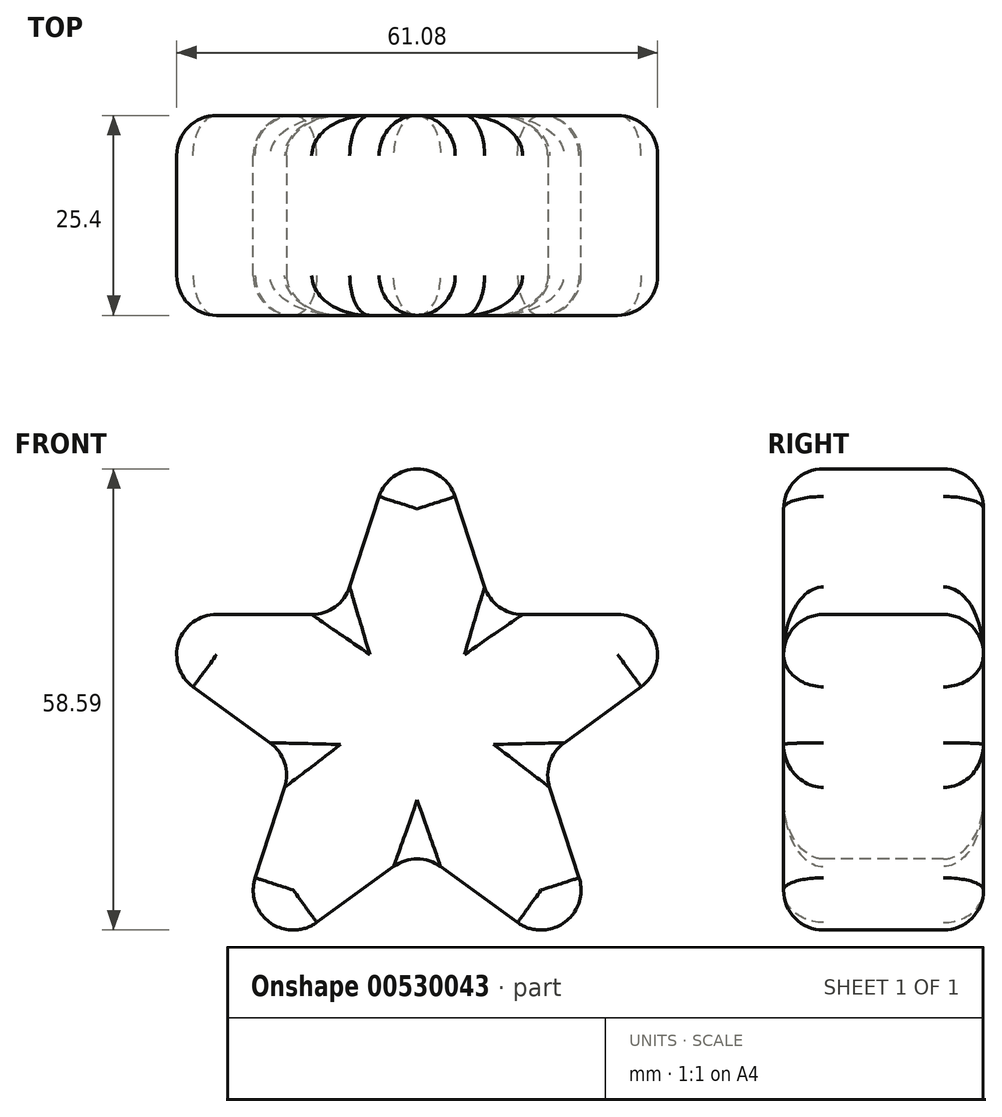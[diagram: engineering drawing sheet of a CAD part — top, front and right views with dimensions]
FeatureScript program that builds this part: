
annotation { "Feature Type Name" : "Feature", "Feature Type Description" : "" }
export const myFeature = defineFeature(function(context is Context, id is Id, definition is map)
    precondition{}
    {
        {
            var Q0;
            Q0=qCreatedBy(makeId("Front.planeOp"),FACE);
            var sketch = newSketch(context, id + "F0", { "sketchPlane" : qUnion([Q0])});
            skLineSegment(sketch, "E0", {"start": v(0, 29.86) * mm, "end": v(-41.1, 0) * mm});
            skLineSegment(sketch, "E1", {"start": v(0, 29.86) * mm, "end": v(41.1, 0) * mm});
            skLineSegment(sketch, "E2", {"start": v(-41.1, 0) * mm, "end": v(-25.4, -48.31) * mm});
            skLineSegment(sketch, "E3", {"start": v(-25.4, -48.31) * mm, "end": v(25.4, -48.31) * mm});
            skLineSegment(sketch, "E4", {"start": v(41.1, 0) * mm, "end": v(25.4, -48.31) * mm});
            skLineSegment(sketch, "E5", {"start": v(-25.4, -48.31) * mm, "end": v(0, 29.86) * mm});
            skLineSegment(sketch, "E6", {"start": v(0, 29.86) * mm, "end": v(25.4, -48.31) * mm});
            skLineSegment(sketch, "E7", {"start": v(25.4, -48.31) * mm, "end": v(-41.1, 0) * mm});
            skLineSegment(sketch, "E8", {"start": v(-41.1, 0) * mm, "end": v(41.1, 0) * mm});
            skLineSegment(sketch, "E9", {"start": v(41.1, 0) * mm, "end": v(-25.4, -48.31) * mm});
            skSolve(sketch);
        }
        {
            var Q0;
            {var subQ1=sQuery(id+"F0.wireOp",EDGE,"E5");var subQ3=sQuery(id+"F0.wireOp",EDGE,"E8");var subQ4=makeQuery(id+"F0.imprint","INTERSECT",VERTEX,{"derivedFrom":[subQ1,subQ3]});Q0=makeQuery(id+"F0.imprint","IMPRINT",FACE,{"disambiguationData":[TD([[makeQuery(id+"F0.imprint","IMPRINT",EDGE,{"disambiguationData":[TD([[subQ4,-1.0]])],"derivedFrom":subQ3}),1.0]])]});}
            var Q1;
            {var subQ0=sQuery(id+"F0.wireOp",EDGE,"E7");var subQ1=sQuery(id+"F0.wireOp",EDGE,"E5");var subQ2=makeQuery(id+"F0.imprint","INTERSECT",VERTEX,{"derivedFrom":[subQ1,subQ0]});Q1=makeQuery(id+"F0.imprint","IMPRINT",FACE,{"disambiguationData":[TD([[makeQuery(id+"F0.imprint","IMPRINT",EDGE,{"disambiguationData":[TD([[subQ2,-1.0]])],"derivedFrom":subQ1}),1.0]])]});}
            var Q2;
            {var subQ1=sQuery(id+"F0.wireOp",EDGE,"E5");var subQ5=sQuery(id+"F0.wireOp",EDGE,"E7");var subQ6=makeQuery(id+"F0.imprint","INTERSECT",VERTEX,{"derivedFrom":[subQ1,subQ5]});Q2=makeQuery(id+"F0.imprint","IMPRINT",FACE,{"disambiguationData":[TD([[makeQuery(id+"F0.imprint","IMPRINT",EDGE,{"disambiguationData":[TD([[subQ6,-1.0]])],"derivedFrom":subQ1}),-1.0]])]});}
            var Q3;
            {var subQ0=sQuery(id+"F0.wireOp",EDGE,"E8");var subQ1=sQuery(id+"F0.wireOp",EDGE,"E6");var subQ2=makeQuery(id+"F0.imprint","INTERSECT",VERTEX,{"derivedFrom":[subQ1,subQ0]});Q3=makeQuery(id+"F0.imprint","IMPRINT",FACE,{"disambiguationData":[TD([[makeQuery(id+"F0.imprint","IMPRINT",EDGE,{"disambiguationData":[TD([[subQ2,-1.0]])],"derivedFrom":subQ1}),1.0]])]});}
            var Q4;
            {var subQ1=sQuery(id+"F0.wireOp",EDGE,"E6");var subQ3=sQuery(id+"F0.wireOp",EDGE,"E9");var subQ4=makeQuery(id+"F0.imprint","INTERSECT",VERTEX,{"derivedFrom":[subQ1,subQ3]});Q4=makeQuery(id+"F0.imprint","IMPRINT",FACE,{"disambiguationData":[TD([[makeQuery(id+"F0.imprint","IMPRINT",EDGE,{"disambiguationData":[TD([[subQ4,-1.0]])],"derivedFrom":subQ3}),1.0]])]});}
            var Q5;
            {var subQ1=sQuery(id+"F0.wireOp",EDGE,"E5");var subQ3=sQuery(id+"F0.wireOp",EDGE,"E7");var subQ4=makeQuery(id+"F0.imprint","INTERSECT",VERTEX,{"derivedFrom":[subQ1,subQ3]});Q5=makeQuery(id+"F0.imprint","IMPRINT",FACE,{"disambiguationData":[TD([[makeQuery(id+"F0.imprint","IMPRINT",EDGE,{"disambiguationData":[TD([[subQ4,1.0]])],"derivedFrom":subQ3}),1.0]])]});}
            extrude(context, id + "F1", {"entities" : qUnion([Q0, Q1, Q2, Q3, Q4, Q5]), "depth" : 25.4 * mm, "offsetDistance" : 25.4 * mm});
        }
        {
            var Q0;
            Q0=makeQuery(id+"F1.opExtrude","CAP_FACE",FACE,{"disambiguationData":[OSD([sQuery(id+"F0.wireOp",EDGE,"E5"),sQuery(id+"F0.wireOp",EDGE,"E6"),sQuery(id+"F0.wireOp",EDGE,"E7"),sQuery(id+"F0.wireOp",EDGE,"E8"),sQuery(id+"F0.wireOp",EDGE,"E9")])],"isStart":true});
            var Q1;
            Q1=makeQuery(id+"F1.opExtrude","CAP_FACE",FACE,{"disambiguationData":[OSD([sQuery(id+"F0.wireOp",EDGE,"E5"),sQuery(id+"F0.wireOp",EDGE,"E6"),sQuery(id+"F0.wireOp",EDGE,"E7"),sQuery(id+"F0.wireOp",EDGE,"E8"),sQuery(id+"F0.wireOp",EDGE,"E9")])],"isStart":false});
            fillet(context, id + "F2", {"entities" : qUnion([Q0, Q1]), "radius" : 5.08 * mm, "tangentPropagation" : true, "allowEdgeOverflow" : false});
        }
        {
            var Q0;
            {var subQ0=sQuery(id+"F0.wireOp",EDGE,"E7");Q0=makeQuery(id+"F1.opExtrude","SWEPT_FACE",FACE,{"disambiguationData":[OSD([subQ0]),TDD([makeQuery(id+"F0.imprint","IMPRINT",EDGE,{"disambiguationData":[TD([[makeQuery(id+"F0.imprint","INTERSECT",VERTEX,{"derivedFrom":[subQ0,sQuery(id+"F0.wireOp",EDGE,"E9")]}),1.0]])],"derivedFrom":subQ0})])]});}
            var Q1;
            {var subQ0=sQuery(id+"F0.wireOp",EDGE,"E9");Q1=makeQuery(id+"F1.opExtrude","SWEPT_FACE",FACE,{"disambiguationData":[OSD([subQ0]),TDD([makeQuery(id+"F0.imprint","IMPRINT",EDGE,{"disambiguationData":[TD([[makeQuery(id+"F0.imprint","INTERSECT",VERTEX,{"derivedFrom":[sQuery(id+"F0.wireOp",EDGE,"E7"),subQ0]}),-1.0]])],"derivedFrom":subQ0})])]});}
            var Q2;
            {var subQ0=sQuery(id+"F0.wireOp",EDGE,"E5");Q2=makeQuery(id+"F1.opExtrude","SWEPT_FACE",FACE,{"disambiguationData":[OSD([subQ0]),TDD([makeQuery(id+"F0.imprint","IMPRINT",EDGE,{"disambiguationData":[TD([[makeQuery(id+"F0.imprint","INTERSECT",VERTEX,{"derivedFrom":[subQ0,sQuery(id+"F0.wireOp",EDGE,"E7")]}),1.0]])],"derivedFrom":subQ0})])]});}
            var Q3;
            {var subQ0=sQuery(id+"F0.wireOp",EDGE,"E7");Q3=makeQuery(id+"F1.opExtrude","SWEPT_FACE",FACE,{"disambiguationData":[OSD([subQ0]),TDD([makeQuery(id+"F0.imprint","IMPRINT",EDGE,{"disambiguationData":[TD([[makeQuery(id+"F0.imprint","INTERSECT",VERTEX,{"derivedFrom":[sQuery(id+"F0.wireOp",EDGE,"E5"),subQ0]}),-1.0]])],"derivedFrom":subQ0})])]});}
            var Q4;
            {var subQ0=sQuery(id+"F0.wireOp",EDGE,"E6");Q4=makeQuery(id+"F1.opExtrude","SWEPT_FACE",FACE,{"disambiguationData":[OSD([subQ0]),TDD([makeQuery(id+"F0.imprint","IMPRINT",EDGE,{"disambiguationData":[TD([[makeQuery(id+"F0.imprint","INTERSECT",VERTEX,{"derivedFrom":[subQ0,sQuery(id+"F0.wireOp",EDGE,"E9")]}),-1.0]])],"derivedFrom":subQ0})])]});}
            var Q5;
            {var subQ0=sQuery(id+"F0.wireOp",EDGE,"E9");Q5=makeQuery(id+"F1.opExtrude","SWEPT_FACE",FACE,{"disambiguationData":[OSD([subQ0]),TDD([makeQuery(id+"F0.imprint","IMPRINT",EDGE,{"disambiguationData":[TD([[makeQuery(id+"F0.imprint","INTERSECT",VERTEX,{"derivedFrom":[sQuery(id+"F0.wireOp",EDGE,"E6"),subQ0]}),1.0]])],"derivedFrom":subQ0})])]});}
            var Q6;
            {var subQ0=sQuery(id+"F0.wireOp",EDGE,"E8");Q6=makeQuery(id+"F1.opExtrude","SWEPT_FACE",FACE,{"disambiguationData":[OSD([subQ0]),TDD([makeQuery(id+"F0.imprint","IMPRINT",EDGE,{"disambiguationData":[TD([[makeQuery(id+"F0.imprint","INTERSECT",VERTEX,{"derivedFrom":[sQuery(id+"F0.wireOp",EDGE,"E6"),subQ0]}),-1.0]])],"derivedFrom":subQ0})])]});}
            fillet(context, id + "F3", {"entities" : qUnion([Q0, Q1, Q2, Q3, Q4, Q5, Q6]), "radius" : 5.08 * mm, "tangentPropagation" : true, "allowEdgeOverflow" : false});
        }
        {
            var Q0;
            {var subQ0=sQuery(id+"F0.wireOp",EDGE,"E5");var subQ1=makeQuery(id+"F0.imprint","IMPRINT",EDGE,{"disambiguationData":[TD([[makeQuery(id+"F0.imprint","INTERSECT",VERTEX,{"derivedFrom":[subQ0,sQuery(id+"F0.wireOp",EDGE,"E8")]}),-1.0]])],"derivedFrom":subQ0});Q0=makeQuery(id+"F2.opFillet","BLEND_EDGE",EDGE,{"blendedFrom":[makeQuery(id+"F1.opExtrude","CAP_EDGE",EDGE,{"disambiguationData":[OSD([subQ0]),TDD([subQ1])],"isStart":true}),makeQuery(id+"F1.opExtrude","SWEPT_FACE",FACE,{"disambiguationData":[OSD([subQ0]),TDD([subQ1])]})],"blendedInto":[makeQuery(id+"F1.opExtrude","SWEPT_FACE",FACE,{"disambiguationData":[OSD([subQ0]),TDD([subQ1])]})]});}
            var Q1;
            {var subQ0=sQuery(id+"F0.wireOp",EDGE,"E5");var subQ1=makeQuery(id+"F0.imprint","IMPRINT",EDGE,{"disambiguationData":[TD([[makeQuery(id+"F0.imprint","INTERSECT",VERTEX,{"derivedFrom":[subQ0,sQuery(id+"F0.wireOp",EDGE,"E8")]}),-1.0]])],"derivedFrom":subQ0});Q1=makeQuery(id+"F2.opFillet","BLEND_EDGE",EDGE,{"blendedFrom":[makeQuery(id+"F1.opExtrude","CAP_EDGE",EDGE,{"disambiguationData":[OSD([subQ0]),TDD([subQ1])],"isStart":false}),makeQuery(id+"F1.opExtrude","SWEPT_FACE",FACE,{"disambiguationData":[OSD([subQ0]),TDD([subQ1])]})],"blendedInto":[makeQuery(id+"F1.opExtrude","SWEPT_FACE",FACE,{"disambiguationData":[OSD([subQ0]),TDD([subQ1])]})]});}
            var Q2;
            {var subQ0=sQuery(id+"F0.wireOp",EDGE,"E5");Q2=makeQuery(id+"F2.opFillet","BLEND_FACE",FACE,{"disambiguationData":[OSD([subQ0]),TDD([makeQuery(id+"F1.opExtrude","CAP_EDGE",EDGE,{"disambiguationData":[OSD([subQ0]),TDD([makeQuery(id+"F0.imprint","IMPRINT",EDGE,{"disambiguationData":[TD([[makeQuery(id+"F0.imprint","INTERSECT",VERTEX,{"derivedFrom":[subQ0,sQuery(id+"F0.wireOp",EDGE,"E8")]}),-1.0]])],"derivedFrom":subQ0})])],"isStart":true})])]});}
            var Q3;
            {var subQ0=sQuery(id+"F0.wireOp",EDGE,"E6");var subQ1=makeQuery(id+"F0.imprint","IMPRINT",EDGE,{"disambiguationData":[TD([[makeQuery(id+"F0.imprint","INTERSECT",VERTEX,{"derivedFrom":[subQ0,sQuery(id+"F0.wireOp",EDGE,"E8")]}),1.0]])],"derivedFrom":subQ0});Q3=makeQuery(id+"F2.opFillet","BLEND_EDGE",EDGE,{"blendedFrom":[makeQuery(id+"F1.opExtrude","CAP_EDGE",EDGE,{"disambiguationData":[OSD([subQ0]),TDD([subQ1])],"isStart":true}),makeQuery(id+"F1.opExtrude","SWEPT_FACE",FACE,{"disambiguationData":[OSD([subQ0]),TDD([subQ1])]})],"blendedInto":[makeQuery(id+"F1.opExtrude","SWEPT_FACE",FACE,{"disambiguationData":[OSD([subQ0]),TDD([subQ1])]})]});}
            var Q4;
            {var subQ0=sQuery(id+"F0.wireOp",EDGE,"E6");Q4=makeQuery(id+"F1.opExtrude","SWEPT_FACE",FACE,{"disambiguationData":[OSD([subQ0]),TDD([makeQuery(id+"F0.imprint","IMPRINT",EDGE,{"disambiguationData":[TD([[makeQuery(id+"F0.imprint","INTERSECT",VERTEX,{"derivedFrom":[subQ0,sQuery(id+"F0.wireOp",EDGE,"E8")]}),1.0]])],"derivedFrom":subQ0})])]});}
            var Q5;
            {var subQ0=sQuery(id+"F0.wireOp",EDGE,"E6");Q5=makeQuery(id+"F2.opFillet","BLEND_FACE",FACE,{"disambiguationData":[OSD([subQ0]),TDD([makeQuery(id+"F1.opExtrude","CAP_EDGE",EDGE,{"disambiguationData":[OSD([subQ0]),TDD([makeQuery(id+"F0.imprint","IMPRINT",EDGE,{"disambiguationData":[TD([[makeQuery(id+"F0.imprint","INTERSECT",VERTEX,{"derivedFrom":[subQ0,sQuery(id+"F0.wireOp",EDGE,"E8")]}),1.0]])],"derivedFrom":subQ0})])],"isStart":false})])]});}
            fillet(context, id + "F4", {"entities" : qUnion([Q0, Q1, Q2, Q3, Q4, Q5]), "radius" : 5.08 * mm, "tangentPropagation" : true, "allowEdgeOverflow" : false});
        }
    });
